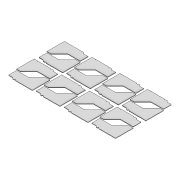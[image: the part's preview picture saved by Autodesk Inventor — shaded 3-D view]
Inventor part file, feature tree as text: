
AUTODESK INVENTOR PART (.ipt)
format: ipt  version: 2022 (Build 260153000, 153)  size: 835,072 bytes
history: native  units: mm
features: extrude x1, sketch x1
ambient origin geometry x8: Origin, YZ Plane, XZ Plane, XY Plane, X Axis, Y Axis, Z Axis, Center Point
bodies: Volumenkörper1 (feature_tree)
feature tree (2):
  extrude  "Extrusion1"  [1 undecoded]
  sketch  "Skizze1"  dims[d0=0.6mm d1=0.0mm]
note: 1 required parameter value undecoded (feature->parameter linkage not recoverable at this tier; creation-order binding heuristic only, values carry confidence <= 0.55)
